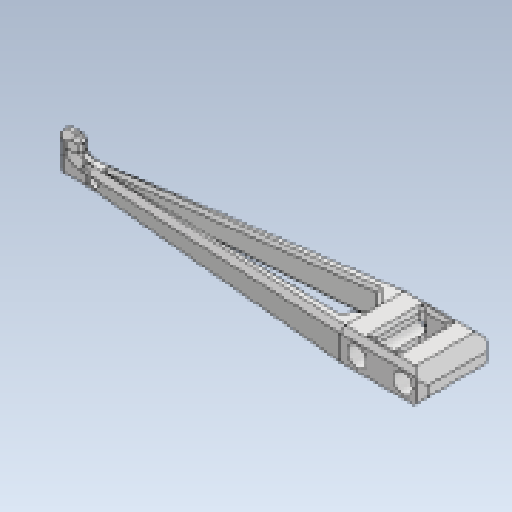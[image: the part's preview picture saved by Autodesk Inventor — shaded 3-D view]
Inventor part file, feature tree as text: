
AUTODESK INVENTOR PART (.ipt)
format: ipt  version: 2023 (Build 270158030, 158C)  size: 296,448 bytes
history: native  units: mm
features: other x4, extrude x1, chamfer x1, sketch x1
ambient origin geometry x8: Origin, YZ Plane, XZ Plane, XY Plane, X Axis, Y Axis, Z Axis, Center Point
bodies: Body1 (feature_tree)
feature tree (7):
  other  "trebuchet-complete-parts.ipt"
  extrude  "Extrusion1"  Depth=3.0mm
  chamfer  "Chamfer1"  Distance=8.0mm
  other  "throw-arm-top::trebuchet-complete-parts.ipt"
  other  "TaggingFeature1"
  sketch  "Sketch1"  dims[d0=10.0mm d1=3.0mm d2=8.0mm d3=2.0mm d4=0.0mm d5=1.5mm d6=2.0mm d7=45.0deg]
  other  "throw-arm-top"
